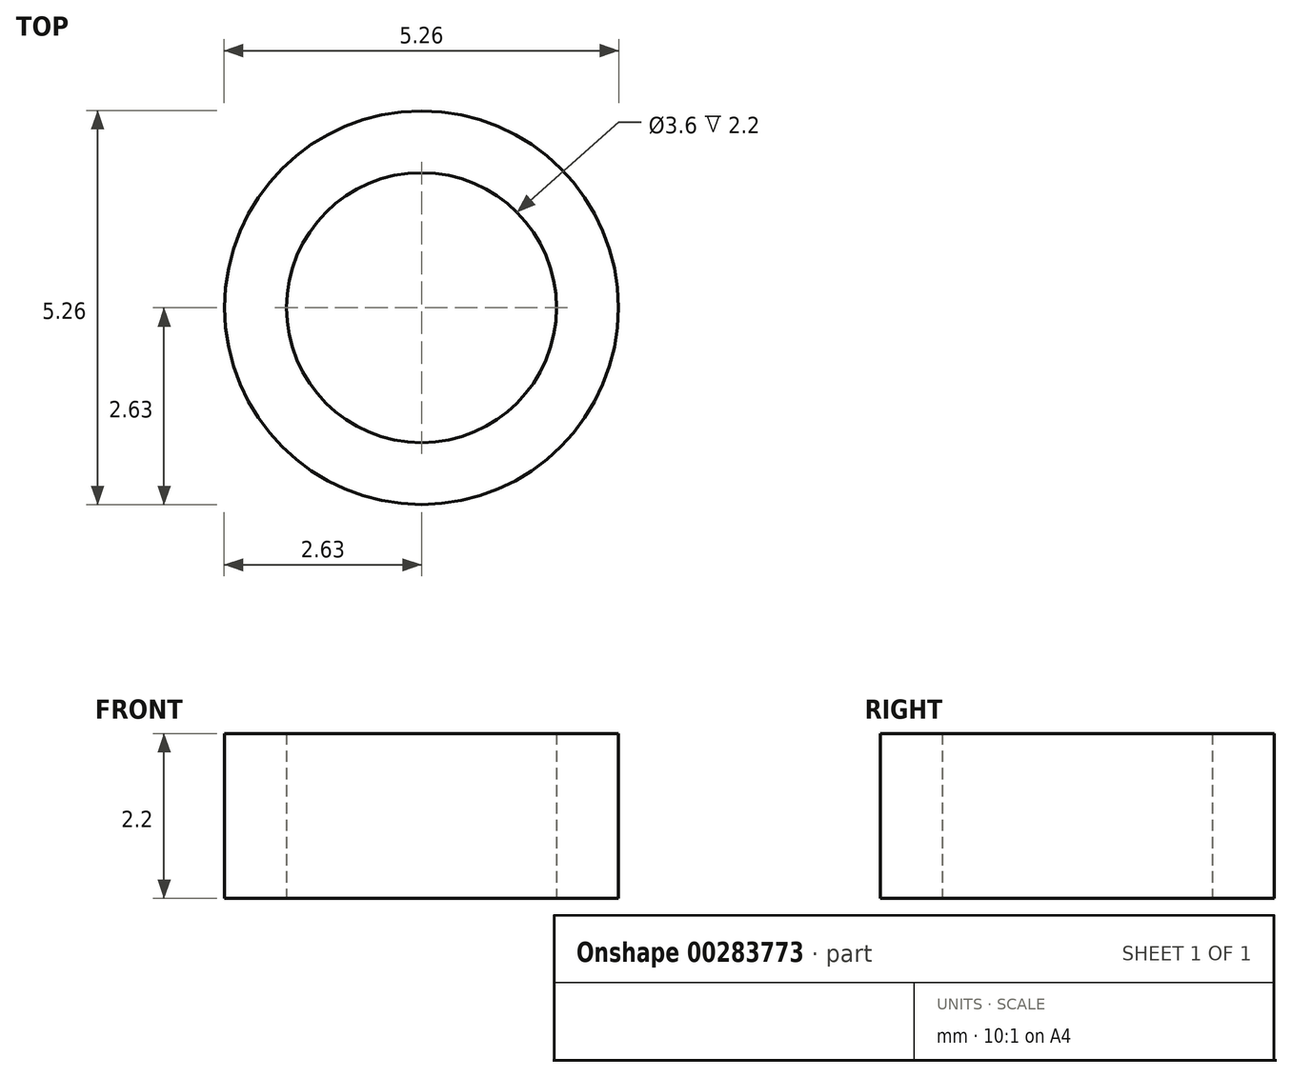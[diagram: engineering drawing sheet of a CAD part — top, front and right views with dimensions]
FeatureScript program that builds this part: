
annotation { "Feature Type Name" : "Feature", "Feature Type Description" : "" }
export const myFeature = defineFeature(function(context is Context, id is Id, definition is map)
    precondition{}
    {
        {
            var Q0;
            Q0=qCreatedBy(makeId("Top.planeOp"),FACE);
            var sketch = newSketch(context, id + "F0", { "sketchPlane" : qUnion([Q0])});
            skCircle(sketch, "E0", {"center": v(0, 0) * mm, "radius": 2.63 * mm});
            skCircle(sketch, "E1", {"center": v(0, 0) * mm, "radius": 1.8 * mm});
            skSolve(sketch);
        }
        {
            var Q0;
            Q0=makeQuery(id+"F0.imprint","IMPRINT",FACE,{"disambiguationData":[TD([[makeQuery(id+"F0.imprint","IMPRINT",EDGE,{"derivedFrom":sQuery(id+"F0.wireOp",EDGE,"E0")}),1.0]])]});
            extrude(context, id + "F1", {"entities" : qUnion([Q0]), "depth" : 2.2 * mm, "offsetDistance" : 25 * mm});
        }
    });
